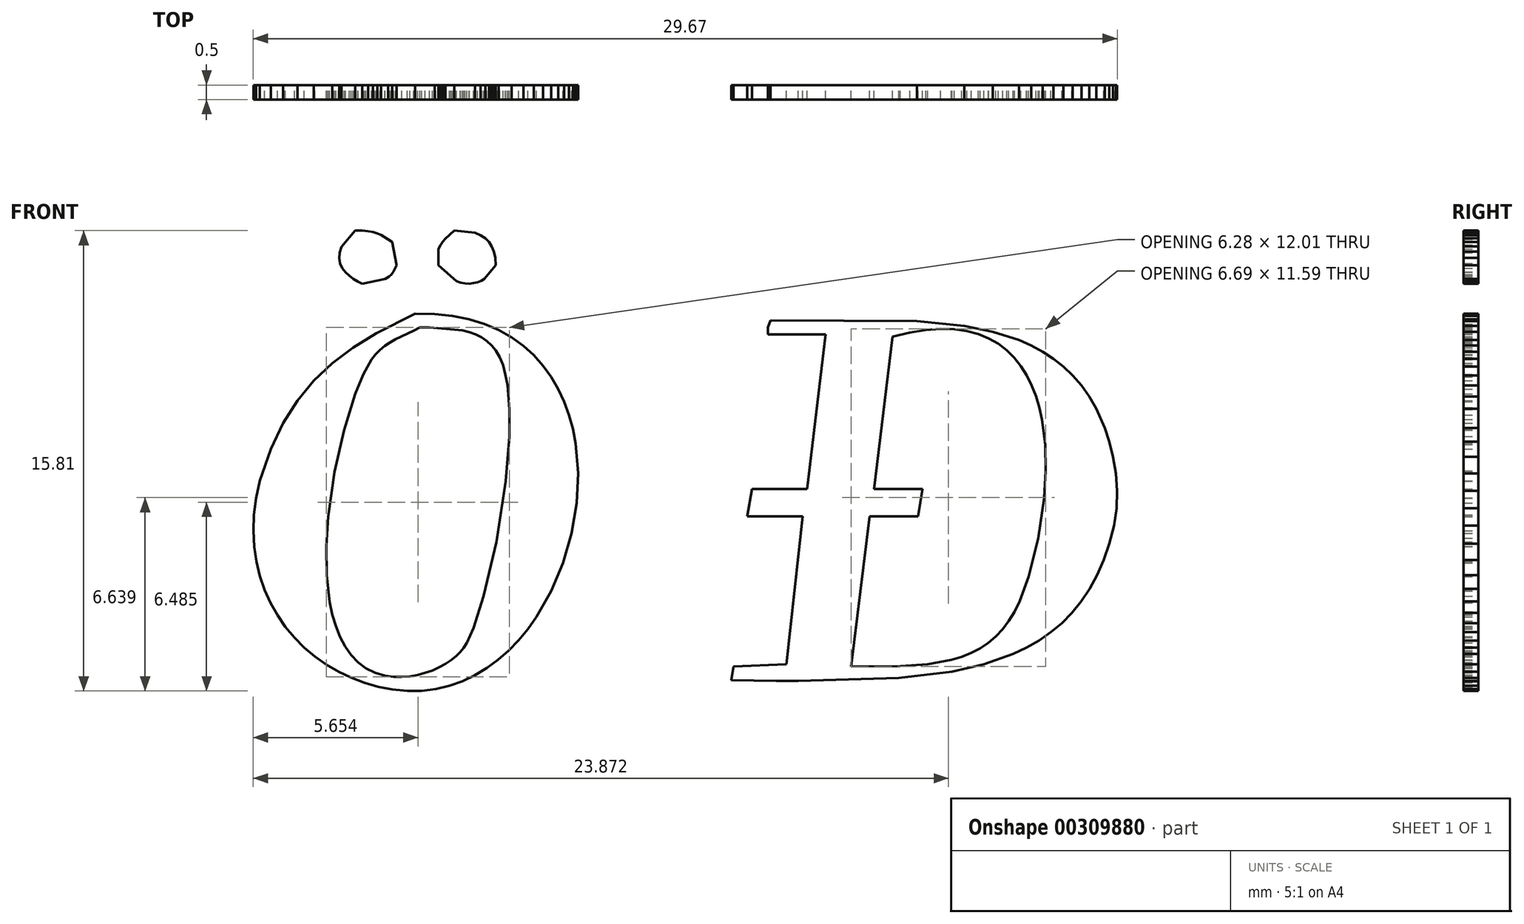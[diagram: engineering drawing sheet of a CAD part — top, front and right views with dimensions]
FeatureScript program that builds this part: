
annotation { "Feature Type Name" : "Feature", "Feature Type Description" : "" }
export const myFeature = defineFeature(function(context is Context, id is Id, definition is map)
    precondition{}
    {
        {
            var Q0;
            Q0=qCreatedBy(makeId("Front.planeOp"),FACE);
            var sketch = newSketch(context, id + "F0", { "sketchPlane" : qUnion([Q0])});
            skPoint(sketch, "E0.0", {"position": v(5.49, 5.53) * mm});
            skPoint(sketch, "E1.0", {"position": v(5.4, 5.3) * mm});
            skPoint(sketch, "E2.0", {"position": v(5.4, 5.06) * mm});
            skPoint(sketch, "E3.0", {"position": v(7.39, 5.06) * mm});
            skPoint(sketch, "E4.0", {"position": v(10.52, 5.52) * mm});
            skPoint(sketch, "E5.0", {"position": v(6.75, -0.25) * mm});
            skPoint(sketch, "E6.0", {"position": v(4.85, -0.25) * mm});
            skPoint(sketch, "E7.0", {"position": v(4.7, -1.2) * mm});
            skPoint(sketch, "E8.0", {"position": v(6.6, -1.2) * mm});
            skPoint(sketch, "E9.0", {"position": v(6.04, -6.27) * mm});
            skPoint(sketch, "E10.0", {"position": v(4.22, -6.35) * mm});
            skPoint(sketch, "E11.0", {"position": v(4.14, -6.82) * mm});
            skPoint(sketch, "E12.0", {"position": v(5.7, -6.84) * mm});
            skPoint(sketch, "E13.0", {"position": v(6.44, -6.84) * mm});
            skPoint(sketch, "E14.0", {"position": v(9.9, -6.75) * mm});
            skPoint(sketch, "E15.0", {"position": v(11.73, -6.52) * mm});
            skPoint(sketch, "E16.0", {"position": v(12.82, -6.27) * mm});
            skPoint(sketch, "E17.0", {"position": v(13.82, -5.92) * mm});
            skPoint(sketch, "E18.0", {"position": v(14.28, -5.7) * mm});
            skPoint(sketch, "E19.0", {"position": v(14.71, -5.46) * mm});
            skPoint(sketch, "E20.0", {"position": v(15.12, -5.17) * mm});
            skPoint(sketch, "E21.0", {"position": v(15.5, -4.86) * mm});
            skPoint(sketch, "E22.0", {"position": v(15.84, -4.5) * mm});
            skPoint(sketch, "E23.0", {"position": v(16.16, -4.12) * mm});
            skPoint(sketch, "E24.0", {"position": v(16.45, -3.69) * mm});
            skPoint(sketch, "E25.0", {"position": v(16.7, -3.21) * mm});
            skPoint(sketch, "E26.0", {"position": v(16.93, -2.7) * mm});
            skPoint(sketch, "E27.0", {"position": v(17.13, -2.13) * mm});
            skPoint(sketch, "E28.0", {"position": v(17.29, -1.52) * mm});
            skPoint(sketch, "E29.0", {"position": v(17.38, -0.92) * mm});
            skPoint(sketch, "E30.0", {"position": v(17.4, -0.31) * mm});
            skPoint(sketch, "E31.0", {"position": v(17.35, 0.28) * mm});
            skPoint(sketch, "E32.0", {"position": v(17.26, 0.85) * mm});
            skPoint(sketch, "E33.0", {"position": v(17.13, 1.37) * mm});
            skPoint(sketch, "E34.0", {"position": v(16.97, 1.84) * mm});
            skPoint(sketch, "E35.0", {"position": v(16.68, 2.5) * mm});
            skPoint(sketch, "E36.0", {"position": v(16.44, 2.92) * mm});
            skPoint(sketch, "E37.0", {"position": v(16.17, 3.3) * mm});
            skPoint(sketch, "E38.0", {"position": v(15.87, 3.64) * mm});
            skPoint(sketch, "E39.0", {"position": v(15.55, 3.95) * mm});
            skPoint(sketch, "E40.0", {"position": v(15.2, 4.22) * mm});
            skPoint(sketch, "E41.0", {"position": v(14.84, 4.46) * mm});
            skPoint(sketch, "E42.0", {"position": v(14.44, 4.67) * mm});
            skPoint(sketch, "E43.0", {"position": v(14.02, 4.86) * mm});
            skPoint(sketch, "E44.0", {"position": v(13.12, 5.15) * mm});
            skPoint(sketch, "E45.0", {"position": v(12.14, 5.35) * mm});
            skPoint(sketch, "E46.0", {"position": v(8.26, -6.35) * mm});
            skPoint(sketch, "E47.0", {"position": v(9.95, -6.34) * mm});
            skPoint(sketch, "E48.0", {"position": v(10.9, -6.27) * mm});
            skPoint(sketch, "E49.0", {"position": v(11.7, -6.12) * mm});
            skPoint(sketch, "E50.0", {"position": v(12.06, -6.01) * mm});
            skPoint(sketch, "E51.0", {"position": v(12.4, -5.88) * mm});
            skPoint(sketch, "E52.0", {"position": v(12.7, -5.73) * mm});
            skPoint(sketch, "E53.0", {"position": v(12.98, -5.54) * mm});
            skPoint(sketch, "E54.0", {"position": v(13.23, -5.32) * mm});
            skPoint(sketch, "E55.0", {"position": v(13.46, -5.07) * mm});
            skPoint(sketch, "E56.0", {"position": v(13.68, -4.79) * mm});
            skPoint(sketch, "E57.0", {"position": v(13.87, -4.47) * mm});
            skPoint(sketch, "E58.0", {"position": v(14.05, -4.1) * mm});
            skPoint(sketch, "E59.0", {"position": v(14.36, -3.26) * mm});
            skPoint(sketch, "E60.0", {"position": v(14.69, -1.94) * mm});
            skPoint(sketch, "E61.0", {"position": v(14.9, -0.56) * mm});
            skPoint(sketch, "E62.0", {"position": v(14.95, 0.36) * mm});
            skPoint(sketch, "E63.0", {"position": v(14.92, 1.27) * mm});
            skPoint(sketch, "E64.0", {"position": v(14.81, 2.13) * mm});
            skPoint(sketch, "E65.0", {"position": v(14.72, 2.54) * mm});
            skPoint(sketch, "E66.0", {"position": v(14.6, 2.93) * mm});
            skPoint(sketch, "E67.0", {"position": v(14.46, 3.3) * mm});
            skPoint(sketch, "E68.0", {"position": v(14.3, 3.64) * mm});
            skPoint(sketch, "E69.0", {"position": v(14.1, 3.96) * mm});
            skPoint(sketch, "E70.0", {"position": v(13.86, 4.25) * mm});
            skPoint(sketch, "E71.0", {"position": v(13.6, 4.5) * mm});
            skPoint(sketch, "E72.0", {"position": v(13.31, 4.73) * mm});
            skPoint(sketch, "E73.0", {"position": v(12.99, 4.92) * mm});
            skPoint(sketch, "E74.0", {"position": v(12.63, 5.07) * mm});
            skPoint(sketch, "E75.0", {"position": v(12.23, 5.17) * mm});
            skPoint(sketch, "E76.0", {"position": v(11.8, 5.23) * mm});
            skPoint(sketch, "E77.0", {"position": v(11.33, 5.25) * mm});
            skPoint(sketch, "E78.0", {"position": v(10.82, 5.2) * mm});
            skPoint(sketch, "E79.0", {"position": v(10.27, 5.12) * mm});
            skPoint(sketch, "E80.0", {"position": v(9.68, 4.98) * mm});
            skPoint(sketch, "E81.0", {"position": v(9.05, -0.25) * mm});
            skPoint(sketch, "E82.0", {"position": v(10.71, -0.25) * mm});
            skPoint(sketch, "E83.0", {"position": v(10.55, -1.2) * mm});
            skPoint(sketch, "E84.0", {"position": v(8.9, -1.2) * mm});
            skPoint(sketch, "E85.0", {"position": v(-5.36, 8.62) * mm});
            skPoint(sketch, "E86.0", {"position": v(-4.65, 8.54) * mm});
            skPoint(sketch, "E87.0", {"position": v(-4.46, 8.45) * mm});
            skPoint(sketch, "E88.0", {"position": v(-4.3, 8.35) * mm});
            skPoint(sketch, "E89.0", {"position": v(-4.18, 8.23) * mm});
            skPoint(sketch, "E90.0", {"position": v(-4.08, 8.08) * mm});
            skPoint(sketch, "E91.0", {"position": v(-4, 7.9) * mm});
            skPoint(sketch, "E92.0", {"position": v(-3.96, 7.69) * mm});
            skPoint(sketch, "E93.0", {"position": v(-3.94, 7.43) * mm});
            skPoint(sketch, "E94.0", {"position": v(-4.33, 6.96) * mm});
            skPoint(sketch, "E95.0", {"position": v(-4.44, 6.9) * mm});
            skPoint(sketch, "E96.0", {"position": v(-4.56, 6.85) * mm});
            skPoint(sketch, "E97.0", {"position": v(-4.7, 6.82) * mm});
            skPoint(sketch, "E98.0", {"position": v(-4.85, 6.8) * mm});
            skPoint(sketch, "E99.0", {"position": v(-5, 6.8) * mm});
            skPoint(sketch, "E100.0", {"position": v(-5.15, 6.83) * mm});
            skPoint(sketch, "E101.0", {"position": v(-5.28, 6.88) * mm});
            skPoint(sketch, "E102.0", {"position": v(-5.92, 7.43) * mm});
            skPoint(sketch, "E103.0", {"position": v(-5.92, 7.99) * mm});
            skPoint(sketch, "E104.0", {"position": v(-5.84, 8.13) * mm});
            skPoint(sketch, "E105.0", {"position": v(-5.76, 8.25) * mm});
            skPoint(sketch, "E106.0", {"position": v(-5.67, 8.34) * mm});
            skPoint(sketch, "E107.0", {"position": v(-7.5, 8.22) * mm});
            skPoint(sketch, "E108.0", {"position": v(-7.34, 7.43) * mm});
            skPoint(sketch, "E109.0", {"position": v(-7.47, 7.2) * mm});
            skPoint(sketch, "E110.0", {"position": v(-7.53, 7.11) * mm});
            skPoint(sketch, "E111.0", {"position": v(-7.62, 7.04) * mm});
            skPoint(sketch, "E112.0", {"position": v(-7.74, 6.96) * mm});
            skPoint(sketch, "E113.0", {"position": v(-8.53, 6.8) * mm});
            skPoint(sketch, "E114.0", {"position": v(-8.68, 6.87) * mm});
            skPoint(sketch, "E115.0", {"position": v(-8.83, 6.96) * mm});
            skPoint(sketch, "E116.0", {"position": v(-8.98, 7.07) * mm});
            skPoint(sketch, "E117.0", {"position": v(-9.1, 7.2) * mm});
            skPoint(sketch, "E118.0", {"position": v(-9.21, 7.33) * mm});
            skPoint(sketch, "E119.0", {"position": v(-9.29, 7.5) * mm});
            skPoint(sketch, "E120.0", {"position": v(-9.32, 7.67) * mm});
            skPoint(sketch, "E121.0", {"position": v(-9.3, 7.86) * mm});
            skPoint(sketch, "E122.0", {"position": v(-9.24, 8.07) * mm});
            skPoint(sketch, "E123.0", {"position": v(-8.77, 8.62) * mm});
            skPoint(sketch, "E124.0", {"position": v(-8.53, 8.62) * mm});
            skPoint(sketch, "E125.0", {"position": v(-8.33, 8.6) * mm});
            skPoint(sketch, "E126.0", {"position": v(-8.16, 8.57) * mm});
            skPoint(sketch, "E127.0", {"position": v(-8.01, 8.53) * mm});
            skPoint(sketch, "E128.0", {"position": v(-7.88, 8.47) * mm});
            skPoint(sketch, "E129.0", {"position": v(-7.64, 8.32) * mm});
            skPoint(sketch, "E130.0", {"position": v(-6.7, 5.77) * mm});
            skPoint(sketch, "E131.0", {"position": v(-6.04, 5.76) * mm});
            skPoint(sketch, "E132.0", {"position": v(-5.43, 5.7) * mm});
            skPoint(sketch, "E133.0", {"position": v(-4.85, 5.58) * mm});
            skPoint(sketch, "E134.0", {"position": v(-4.32, 5.41) * mm});
            skPoint(sketch, "E135.0", {"position": v(-3.84, 5.2) * mm});
            skPoint(sketch, "E136.0", {"position": v(-3.4, 4.95) * mm});
            skPoint(sketch, "E137.0", {"position": v(-3, 4.66) * mm});
            skPoint(sketch, "E138.0", {"position": v(-2.63, 4.34) * mm});
            skPoint(sketch, "E139.0", {"position": v(-2.31, 3.98) * mm});
            skPoint(sketch, "E140.0", {"position": v(-2.03, 3.6) * mm});
            skPoint(sketch, "E141.0", {"position": v(-1.8, 3.18) * mm});
            skPoint(sketch, "E142.0", {"position": v(-1.6, 2.74) * mm});
            skPoint(sketch, "E143.0", {"position": v(-1.42, 2.28) * mm});
            skPoint(sketch, "E144.0", {"position": v(-1.3, 1.8) * mm});
            skPoint(sketch, "E145.0", {"position": v(-1.2, 1.31) * mm});
            skPoint(sketch, "E146.0", {"position": v(-1.12, 0.3) * mm});
            skPoint(sketch, "E147.0", {"position": v(-1.16, -0.74) * mm});
            skPoint(sketch, "E148.0", {"position": v(-1.34, -1.78) * mm});
            skPoint(sketch, "E149.0", {"position": v(-1.63, -2.8) * mm});
            skPoint(sketch, "E150.0", {"position": v(-2.04, -3.76) * mm});
            skPoint(sketch, "E151.0", {"position": v(-2.55, -4.65) * mm});
            skPoint(sketch, "E152.0", {"position": v(-2.84, -5.06) * mm});
            skPoint(sketch, "E153.0", {"position": v(-3.16, -5.45) * mm});
            skPoint(sketch, "E154.0", {"position": v(-3.5, -5.8) * mm});
            skPoint(sketch, "E155.0", {"position": v(-3.87, -6.12) * mm});
            skPoint(sketch, "E156.0", {"position": v(-4.25, -6.4) * mm});
            skPoint(sketch, "E157.0", {"position": v(-4.66, -6.65) * mm});
            skPoint(sketch, "E158.0", {"position": v(-5.09, -6.86) * mm});
            skPoint(sketch, "E159.0", {"position": v(-5.54, -7.02) * mm});
            skPoint(sketch, "E160.0", {"position": v(-6, -7.13) * mm});
            skPoint(sketch, "E161.0", {"position": v(-6.49, -7.19) * mm});
            skPoint(sketch, "E162.0", {"position": v(-6.99, -7.2) * mm});
            skPoint(sketch, "E163.0", {"position": v(-7.5, -7.14) * mm});
            skPoint(sketch, "E164.0", {"position": v(-7.99, -7.04) * mm});
            skPoint(sketch, "E165.0", {"position": v(-8.46, -6.9) * mm});
            skPoint(sketch, "E166.0", {"position": v(-8.91, -6.74) * mm});
            skPoint(sketch, "E167.0", {"position": v(-9.35, -6.53) * mm});
            skPoint(sketch, "E168.0", {"position": v(-9.76, -6.28) * mm});
            skPoint(sketch, "E169.0", {"position": v(-10.15, -6) * mm});
            skPoint(sketch, "E170.0", {"position": v(-10.52, -5.7) * mm});
            skPoint(sketch, "E171.0", {"position": v(-10.86, -5.36) * mm});
            skPoint(sketch, "E172.0", {"position": v(-11.17, -4.99) * mm});
            skPoint(sketch, "E173.0", {"position": v(-11.44, -4.59) * mm});
            skPoint(sketch, "E174.0", {"position": v(-11.68, -4.17) * mm});
            skPoint(sketch, "E175.0", {"position": v(-11.88, -3.72) * mm});
            skPoint(sketch, "E176.0", {"position": v(-12.04, -3.24) * mm});
            skPoint(sketch, "E177.0", {"position": v(-12.16, -2.75) * mm});
            skPoint(sketch, "E178.0", {"position": v(-6.55, 5.3) * mm});
            skPoint(sketch, "E179.0", {"position": v(-6.22, 5.3) * mm});
            skPoint(sketch, "E180.0", {"position": v(-5.09, 5.2) * mm});
            skPoint(sketch, "E181.0", {"position": v(-4.85, 5.13) * mm});
            skPoint(sketch, "E182.0", {"position": v(-4.63, 5.05) * mm});
            skPoint(sketch, "E183.0", {"position": v(-4.43, 4.95) * mm});
            skPoint(sketch, "E184.0", {"position": v(-4.25, 4.83) * mm});
            skPoint(sketch, "E185.0", {"position": v(-4.08, 4.68) * mm});
            skPoint(sketch, "E186.0", {"position": v(-3.94, 4.5) * mm});
            skPoint(sketch, "E187.0", {"position": v(-3.8, 4.27) * mm});
            skPoint(sketch, "E188.0", {"position": v(-3.7, 4) * mm});
            skPoint(sketch, "E189.0", {"position": v(-3.6, 3.67) * mm});
            skPoint(sketch, "E190.0", {"position": v(-3.54, 3.31) * mm});
            skPoint(sketch, "E191.0", {"position": v(-3.48, 2.48) * mm});
            skPoint(sketch, "E192.0", {"position": v(-3.48, 1.55) * mm});
            skPoint(sketch, "E193.0", {"position": v(-3.6, 0.02) * mm});
            skPoint(sketch, "E194.0", {"position": v(-3.92, -2.06) * mm});
            skPoint(sketch, "E195.0", {"position": v(-4.36, -3.93) * mm});
            skPoint(sketch, "E196.0", {"position": v(-4.71, -5.02) * mm});
            skPoint(sketch, "E197.0", {"position": v(-4.94, -5.54) * mm});
            skPoint(sketch, "E198.0", {"position": v(-5.05, -5.71) * mm});
            skPoint(sketch, "E199.0", {"position": v(-5.16, -5.86) * mm});
            skPoint(sketch, "E200.0", {"position": v(-5.3, -6) * mm});
            skPoint(sketch, "E201.0", {"position": v(-5.48, -6.13) * mm});
            skPoint(sketch, "E202.0", {"position": v(-5.67, -6.26) * mm});
            skPoint(sketch, "E203.0", {"position": v(-5.89, -6.38) * mm});
            skPoint(sketch, "E204.0", {"position": v(-6.12, -6.48) * mm});
            skPoint(sketch, "E205.0", {"position": v(-6.37, -6.57) * mm});
            skPoint(sketch, "E206.0", {"position": v(-6.63, -6.64) * mm});
            skPoint(sketch, "E207.0", {"position": v(-6.9, -6.69) * mm});
            skPoint(sketch, "E208.0", {"position": v(-7.17, -6.7) * mm});
            skPoint(sketch, "E209.0", {"position": v(-7.46, -6.7) * mm});
            skPoint(sketch, "E210.0", {"position": v(-7.74, -6.66) * mm});
            skPoint(sketch, "E211.0", {"position": v(-8.09, -6.57) * mm});
            skPoint(sketch, "E212.0", {"position": v(-8.4, -6.41) * mm});
            skPoint(sketch, "E213.0", {"position": v(-8.67, -6.21) * mm});
            skPoint(sketch, "E214.0", {"position": v(-8.91, -5.96) * mm});
            skPoint(sketch, "E215.0", {"position": v(-9.12, -5.67) * mm});
            skPoint(sketch, "E216.0", {"position": v(-9.3, -5.33) * mm});
            skPoint(sketch, "E217.0", {"position": v(-9.44, -4.97) * mm});
            skPoint(sketch, "E218.0", {"position": v(-9.55, -4.57) * mm});
            skPoint(sketch, "E219.0", {"position": v(-9.64, -4.14) * mm});
            skPoint(sketch, "E220.0", {"position": v(-9.74, -3.22) * mm});
            skPoint(sketch, "E221.0", {"position": v(-9.76, -2.23) * mm});
            skPoint(sketch, "E222.0", {"position": v(-9.7, -1.2) * mm});
            skPoint(sketch, "E223.0", {"position": v(-9.48, 0.33) * mm});
            skPoint(sketch, "E224.0", {"position": v(-9.15, 1.77) * mm});
            skPoint(sketch, "E225.0", {"position": v(-8.76, 3.01) * mm});
            skPoint(sketch, "E226.0", {"position": v(-8.49, 3.68) * mm});
            skPoint(sketch, "E227.0", {"position": v(-8.21, 4.19) * mm});
            skPoint(sketch, "E228.0", {"position": v(-8.08, 4.37) * mm});
            skPoint(sketch, "E229.0", {"position": v(-7.92, 4.53) * mm});
            skPoint(sketch, "E230.0", {"position": v(-7.76, 4.66) * mm});
            skPoint(sketch, "E231.0", {"position": v(-7.58, 4.78) * mm});
            skPoint(sketch, "E232.0", {"position": v(-7.39, 4.89) * mm});
            skPoint(sketch, "E233.0", {"position": v(-6.77, 5.19) * mm});
            skPoint(sketch, "E234.0", {"position": v(-12.24, -2.23) * mm});
            skPoint(sketch, "E235.0", {"position": v(-12.27, -1.7) * mm});
            skPoint(sketch, "E236.0", {"position": v(-12.24, -1.14) * mm});
            skPoint(sketch, "E237.0", {"position": v(-12.17, -0.57) * mm});
            skPoint(sketch, "E238.0", {"position": v(-12.04, 0.02) * mm});
            skPoint(sketch, "E239.0", {"position": v(-11.67, 1.12) * mm});
            skPoint(sketch, "E240.0", {"position": v(-11.24, 2) * mm});
            skPoint(sketch, "E241.0", {"position": v(-10.75, 2.79) * mm});
            skPoint(sketch, "E242.0", {"position": v(-10.19, 3.47) * mm});
            skPoint(sketch, "E243.0", {"position": v(-9.55, 4.07) * mm});
            skPoint(sketch, "E244.0", {"position": v(-8.84, 4.6) * mm});
            skPoint(sketch, "E245.0", {"position": v(-8.05, 5.09) * mm});
            skLineSegment(sketch, "E246", {"start": v(13.12, 5.15) * mm, "end": v(14.02, 4.86) * mm});
            skLineSegment(sketch, "E247", {"start": v(14.02, 4.86) * mm, "end": v(14.44, 4.67) * mm});
            skLineSegment(sketch, "E248", {"start": v(14.44, 4.67) * mm, "end": v(14.84, 4.46) * mm});
            skLineSegment(sketch, "E249", {"start": v(14.84, 4.46) * mm, "end": v(15.2, 4.22) * mm});
            skLineSegment(sketch, "E250", {"start": v(15.2, 4.22) * mm, "end": v(15.55, 3.95) * mm});
            skLineSegment(sketch, "E251", {"start": v(15.55, 3.95) * mm, "end": v(15.87, 3.64) * mm});
            skLineSegment(sketch, "E252", {"start": v(15.87, 3.64) * mm, "end": v(16.17, 3.3) * mm});
            skLineSegment(sketch, "E253", {"start": v(16.17, 3.3) * mm, "end": v(16.44, 2.92) * mm});
            skLineSegment(sketch, "E254", {"start": v(16.44, 2.92) * mm, "end": v(16.68, 2.5) * mm});
            skLineSegment(sketch, "E255", {"start": v(16.68, 2.5) * mm, "end": v(16.97, 1.84) * mm});
            skLineSegment(sketch, "E256", {"start": v(16.97, 1.84) * mm, "end": v(17.13, 1.37) * mm});
            skLineSegment(sketch, "E257", {"start": v(17.13, 1.37) * mm, "end": v(17.26, 0.85) * mm});
            skLineSegment(sketch, "E258", {"start": v(17.26, 0.85) * mm, "end": v(17.35, 0.28) * mm});
            skLineSegment(sketch, "E259", {"start": v(17.35, 0.28) * mm, "end": v(17.4, -0.31) * mm});
            skLineSegment(sketch, "E260", {"start": v(17.4, -0.31) * mm, "end": v(17.38, -0.92) * mm});
            skLineSegment(sketch, "E261", {"start": v(17.38, -0.92) * mm, "end": v(17.29, -1.52) * mm});
            skLineSegment(sketch, "E262", {"start": v(17.29, -1.52) * mm, "end": v(17.13, -2.13) * mm});
            skLineSegment(sketch, "E263", {"start": v(17.13, -2.13) * mm, "end": v(16.93, -2.7) * mm});
            skLineSegment(sketch, "E264", {"start": v(16.93, -2.7) * mm, "end": v(16.7, -3.21) * mm});
            skLineSegment(sketch, "E265", {"start": v(16.7, -3.21) * mm, "end": v(16.45, -3.69) * mm});
            skLineSegment(sketch, "E266", {"start": v(16.45, -3.69) * mm, "end": v(16.16, -4.12) * mm});
            skLineSegment(sketch, "E267", {"start": v(16.16, -4.12) * mm, "end": v(15.84, -4.5) * mm});
            skLineSegment(sketch, "E268", {"start": v(15.84, -4.5) * mm, "end": v(15.5, -4.86) * mm});
            skLineSegment(sketch, "E269", {"start": v(15.5, -4.86) * mm, "end": v(15.12, -5.17) * mm});
            skLineSegment(sketch, "E270", {"start": v(15.12, -5.17) * mm, "end": v(14.71, -5.46) * mm});
            skLineSegment(sketch, "E271", {"start": v(14.71, -5.46) * mm, "end": v(14.28, -5.7) * mm});
            skLineSegment(sketch, "E272", {"start": v(14.28, -5.7) * mm, "end": v(13.82, -5.92) * mm});
            skLineSegment(sketch, "E273", {"start": v(13.82, -5.92) * mm, "end": v(12.82, -6.27) * mm});
            skLineSegment(sketch, "E274", {"start": v(12.82, -6.27) * mm, "end": v(11.73, -6.52) * mm});
            skLineSegment(sketch, "E275", {"start": v(11.73, -6.52) * mm, "end": v(9.9, -6.75) * mm});
            skLineSegment(sketch, "E276", {"start": v(9.9, -6.75) * mm, "end": v(6.44, -6.84) * mm});
            skLineSegment(sketch, "E277", {"start": v(6.44, -6.84) * mm, "end": v(5.7, -6.84) * mm});
            skLineSegment(sketch, "E278", {"start": v(5.7, -6.84) * mm, "end": v(4.14, -6.82) * mm});
            skLineSegment(sketch, "E279", {"start": v(4.14, -6.82) * mm, "end": v(4.22, -6.35) * mm});
            skLineSegment(sketch, "E280", {"start": v(4.22, -6.35) * mm, "end": v(6.04, -6.27) * mm});
            skLineSegment(sketch, "E281", {"start": v(6.04, -6.27) * mm, "end": v(6.6, -1.2) * mm});
            skLineSegment(sketch, "E282", {"start": v(6.6, -1.2) * mm, "end": v(4.7, -1.2) * mm});
            skLineSegment(sketch, "E283", {"start": v(4.7, -1.2) * mm, "end": v(4.85, -0.25) * mm});
            skLineSegment(sketch, "E284", {"start": v(4.85, -0.25) * mm, "end": v(6.75, -0.25) * mm});
            skLineSegment(sketch, "E285", {"start": v(6.75, -0.25) * mm, "end": v(7.39, 5.06) * mm});
            skLineSegment(sketch, "E286", {"start": v(7.39, 5.06) * mm, "end": v(5.4, 5.06) * mm});
            skLineSegment(sketch, "E287", {"start": v(5.4, 5.06) * mm, "end": v(5.4, 5.3) * mm});
            skLineSegment(sketch, "E288", {"start": v(5.4, 5.3) * mm, "end": v(5.49, 5.53) * mm});
            skLineSegment(sketch, "E289", {"start": v(5.49, 5.53) * mm, "end": v(10.52, 5.52) * mm});
            skLineSegment(sketch, "E290", {"start": v(10.52, 5.52) * mm, "end": v(12.14, 5.35) * mm});
            skLineSegment(sketch, "E291", {"start": v(12.14, 5.35) * mm, "end": v(13.12, 5.15) * mm});
            skLineSegment(sketch, "E292", {"start": v(9.05, -0.25) * mm, "end": v(9.68, 4.98) * mm});
            skLineSegment(sketch, "E293", {"start": v(9.68, 4.98) * mm, "end": v(10.27, 5.12) * mm});
            skLineSegment(sketch, "E294", {"start": v(10.27, 5.12) * mm, "end": v(10.82, 5.2) * mm});
            skLineSegment(sketch, "E295", {"start": v(10.82, 5.2) * mm, "end": v(11.33, 5.25) * mm});
            skLineSegment(sketch, "E296", {"start": v(11.33, 5.25) * mm, "end": v(11.8, 5.23) * mm});
            skLineSegment(sketch, "E297", {"start": v(11.8, 5.23) * mm, "end": v(12.23, 5.17) * mm});
            skLineSegment(sketch, "E298", {"start": v(12.23, 5.17) * mm, "end": v(12.63, 5.07) * mm});
            skLineSegment(sketch, "E299", {"start": v(12.63, 5.07) * mm, "end": v(12.99, 4.92) * mm});
            skLineSegment(sketch, "E300", {"start": v(12.99, 4.92) * mm, "end": v(13.31, 4.73) * mm});
            skLineSegment(sketch, "E301", {"start": v(13.31, 4.73) * mm, "end": v(13.6, 4.5) * mm});
            skLineSegment(sketch, "E302", {"start": v(13.6, 4.5) * mm, "end": v(13.86, 4.25) * mm});
            skLineSegment(sketch, "E303", {"start": v(13.86, 4.25) * mm, "end": v(14.1, 3.96) * mm});
            skLineSegment(sketch, "E304", {"start": v(14.1, 3.96) * mm, "end": v(14.3, 3.64) * mm});
            skLineSegment(sketch, "E305", {"start": v(14.3, 3.64) * mm, "end": v(14.46, 3.3) * mm});
            skLineSegment(sketch, "E306", {"start": v(14.46, 3.3) * mm, "end": v(14.6, 2.93) * mm});
            skLineSegment(sketch, "E307", {"start": v(14.6, 2.93) * mm, "end": v(14.72, 2.54) * mm});
            skLineSegment(sketch, "E308", {"start": v(14.72, 2.54) * mm, "end": v(14.81, 2.13) * mm});
            skLineSegment(sketch, "E309", {"start": v(14.81, 2.13) * mm, "end": v(14.92, 1.27) * mm});
            skLineSegment(sketch, "E310", {"start": v(14.92, 1.27) * mm, "end": v(14.95, 0.36) * mm});
            skLineSegment(sketch, "E311", {"start": v(14.95, 0.36) * mm, "end": v(14.9, -0.56) * mm});
            skLineSegment(sketch, "E312", {"start": v(14.9, -0.56) * mm, "end": v(14.69, -1.94) * mm});
            skLineSegment(sketch, "E313", {"start": v(14.69, -1.94) * mm, "end": v(14.36, -3.26) * mm});
            skLineSegment(sketch, "E314", {"start": v(14.36, -3.26) * mm, "end": v(14.05, -4.1) * mm});
            skLineSegment(sketch, "E315", {"start": v(14.05, -4.1) * mm, "end": v(13.87, -4.47) * mm});
            skLineSegment(sketch, "E316", {"start": v(13.87, -4.47) * mm, "end": v(13.68, -4.79) * mm});
            skLineSegment(sketch, "E317", {"start": v(13.68, -4.79) * mm, "end": v(13.46, -5.07) * mm});
            skLineSegment(sketch, "E318", {"start": v(13.46, -5.07) * mm, "end": v(13.23, -5.32) * mm});
            skLineSegment(sketch, "E319", {"start": v(13.23, -5.32) * mm, "end": v(12.98, -5.54) * mm});
            skLineSegment(sketch, "E320", {"start": v(12.98, -5.54) * mm, "end": v(12.7, -5.73) * mm});
            skLineSegment(sketch, "E321", {"start": v(12.7, -5.73) * mm, "end": v(12.4, -5.88) * mm});
            skLineSegment(sketch, "E322", {"start": v(12.4, -5.88) * mm, "end": v(12.06, -6.01) * mm});
            skLineSegment(sketch, "E323", {"start": v(12.06, -6.01) * mm, "end": v(11.7, -6.12) * mm});
            skLineSegment(sketch, "E324", {"start": v(11.7, -6.12) * mm, "end": v(10.9, -6.27) * mm});
            skLineSegment(sketch, "E325", {"start": v(10.9, -6.27) * mm, "end": v(9.95, -6.34) * mm});
            skLineSegment(sketch, "E326", {"start": v(9.95, -6.34) * mm, "end": v(8.26, -6.35) * mm});
            skLineSegment(sketch, "E327", {"start": v(8.26, -6.35) * mm, "end": v(8.9, -1.2) * mm});
            skLineSegment(sketch, "E328", {"start": v(8.9, -1.2) * mm, "end": v(10.55, -1.2) * mm});
            skLineSegment(sketch, "E329", {"start": v(10.55, -1.2) * mm, "end": v(10.71, -0.25) * mm});
            skLineSegment(sketch, "E330", {"start": v(10.71, -0.25) * mm, "end": v(9.05, -0.25) * mm});
            skLineSegment(sketch, "E331", {"start": v(-5.36, 8.62) * mm, "end": v(-4.65, 8.54) * mm});
            skLineSegment(sketch, "E332", {"start": v(-4.65, 8.54) * mm, "end": v(-4.46, 8.45) * mm});
            skLineSegment(sketch, "E333", {"start": v(-4.46, 8.45) * mm, "end": v(-4.3, 8.35) * mm});
            skLineSegment(sketch, "E334", {"start": v(-4.3, 8.35) * mm, "end": v(-4.18, 8.23) * mm});
            skLineSegment(sketch, "E335", {"start": v(-4.18, 8.23) * mm, "end": v(-4.08, 8.08) * mm});
            skLineSegment(sketch, "E336", {"start": v(-4.08, 8.08) * mm, "end": v(-4, 7.9) * mm});
            skLineSegment(sketch, "E337", {"start": v(-4, 7.9) * mm, "end": v(-3.96, 7.69) * mm});
            skLineSegment(sketch, "E338", {"start": v(-3.96, 7.69) * mm, "end": v(-3.94, 7.43) * mm});
            skLineSegment(sketch, "E339", {"start": v(-3.94, 7.43) * mm, "end": v(-4.33, 6.96) * mm});
            skLineSegment(sketch, "E340", {"start": v(-4.33, 6.96) * mm, "end": v(-4.44, 6.9) * mm});
            skLineSegment(sketch, "E341", {"start": v(-4.44, 6.9) * mm, "end": v(-4.56, 6.85) * mm});
            skLineSegment(sketch, "E342", {"start": v(-4.56, 6.85) * mm, "end": v(-4.7, 6.82) * mm});
            skLineSegment(sketch, "E343", {"start": v(-4.7, 6.82) * mm, "end": v(-4.85, 6.8) * mm});
            skLineSegment(sketch, "E344", {"start": v(-4.85, 6.8) * mm, "end": v(-5, 6.8) * mm});
            skLineSegment(sketch, "E345", {"start": v(-5, 6.8) * mm, "end": v(-5.15, 6.83) * mm});
            skLineSegment(sketch, "E346", {"start": v(-5.15, 6.83) * mm, "end": v(-5.28, 6.88) * mm});
            skLineSegment(sketch, "E347", {"start": v(-5.28, 6.88) * mm, "end": v(-5.92, 7.43) * mm});
            skLineSegment(sketch, "E348", {"start": v(-5.92, 7.43) * mm, "end": v(-5.92, 7.99) * mm});
            skLineSegment(sketch, "E349", {"start": v(-5.92, 7.99) * mm, "end": v(-5.84, 8.13) * mm});
            skLineSegment(sketch, "E350", {"start": v(-5.84, 8.13) * mm, "end": v(-5.76, 8.25) * mm});
            skLineSegment(sketch, "E351", {"start": v(-5.76, 8.25) * mm, "end": v(-5.67, 8.34) * mm});
            skLineSegment(sketch, "E352", {"start": v(-5.67, 8.34) * mm, "end": v(-5.36, 8.62) * mm});
            skLineSegment(sketch, "E353", {"start": v(-7.5, 8.22) * mm, "end": v(-7.34, 7.43) * mm});
            skLineSegment(sketch, "E354", {"start": v(-7.34, 7.43) * mm, "end": v(-7.47, 7.2) * mm});
            skLineSegment(sketch, "E355", {"start": v(-7.47, 7.2) * mm, "end": v(-7.53, 7.11) * mm});
            skLineSegment(sketch, "E356", {"start": v(-7.53, 7.11) * mm, "end": v(-7.62, 7.04) * mm});
            skLineSegment(sketch, "E357", {"start": v(-7.62, 7.04) * mm, "end": v(-7.74, 6.96) * mm});
            skLineSegment(sketch, "E358", {"start": v(-7.74, 6.96) * mm, "end": v(-8.53, 6.8) * mm});
            skLineSegment(sketch, "E359", {"start": v(-8.53, 6.8) * mm, "end": v(-8.68, 6.87) * mm});
            skLineSegment(sketch, "E360", {"start": v(-8.68, 6.87) * mm, "end": v(-8.83, 6.96) * mm});
            skLineSegment(sketch, "E361", {"start": v(-8.83, 6.96) * mm, "end": v(-8.98, 7.07) * mm});
            skLineSegment(sketch, "E362", {"start": v(-8.98, 7.07) * mm, "end": v(-9.1, 7.2) * mm});
            skLineSegment(sketch, "E363", {"start": v(-9.1, 7.2) * mm, "end": v(-9.21, 7.33) * mm});
            skLineSegment(sketch, "E364", {"start": v(-9.21, 7.33) * mm, "end": v(-9.29, 7.5) * mm});
            skLineSegment(sketch, "E365", {"start": v(-9.29, 7.5) * mm, "end": v(-9.32, 7.67) * mm});
            skLineSegment(sketch, "E366", {"start": v(-9.32, 7.67) * mm, "end": v(-9.3, 7.86) * mm});
            skLineSegment(sketch, "E367", {"start": v(-9.3, 7.86) * mm, "end": v(-9.24, 8.07) * mm});
            skLineSegment(sketch, "E368", {"start": v(-9.24, 8.07) * mm, "end": v(-8.77, 8.62) * mm});
            skLineSegment(sketch, "E369", {"start": v(-8.77, 8.62) * mm, "end": v(-8.53, 8.62) * mm});
            skLineSegment(sketch, "E370", {"start": v(-8.53, 8.62) * mm, "end": v(-8.33, 8.6) * mm});
            skLineSegment(sketch, "E371", {"start": v(-8.33, 8.6) * mm, "end": v(-8.16, 8.57) * mm});
            skLineSegment(sketch, "E372", {"start": v(-8.16, 8.57) * mm, "end": v(-8.01, 8.53) * mm});
            skLineSegment(sketch, "E373", {"start": v(-8.01, 8.53) * mm, "end": v(-7.88, 8.47) * mm});
            skLineSegment(sketch, "E374", {"start": v(-7.88, 8.47) * mm, "end": v(-7.64, 8.32) * mm});
            skLineSegment(sketch, "E375", {"start": v(-7.64, 8.32) * mm, "end": v(-7.5, 8.22) * mm});
            skLineSegment(sketch, "E376", {"start": v(-3.84, 5.2) * mm, "end": v(-3.4, 4.95) * mm});
            skLineSegment(sketch, "E377", {"start": v(-3.4, 4.95) * mm, "end": v(-3, 4.66) * mm});
            skLineSegment(sketch, "E378", {"start": v(-3, 4.66) * mm, "end": v(-2.63, 4.34) * mm});
            skLineSegment(sketch, "E379", {"start": v(-2.63, 4.34) * mm, "end": v(-2.31, 3.98) * mm});
            skLineSegment(sketch, "E380", {"start": v(-2.31, 3.98) * mm, "end": v(-2.03, 3.6) * mm});
            skLineSegment(sketch, "E381", {"start": v(-2.03, 3.6) * mm, "end": v(-1.8, 3.18) * mm});
            skLineSegment(sketch, "E382", {"start": v(-1.8, 3.18) * mm, "end": v(-1.6, 2.74) * mm});
            skLineSegment(sketch, "E383", {"start": v(-1.6, 2.74) * mm, "end": v(-1.42, 2.28) * mm});
            skLineSegment(sketch, "E384", {"start": v(-1.42, 2.28) * mm, "end": v(-1.3, 1.8) * mm});
            skLineSegment(sketch, "E385", {"start": v(-1.3, 1.8) * mm, "end": v(-1.2, 1.31) * mm});
            skLineSegment(sketch, "E386", {"start": v(-1.2, 1.31) * mm, "end": v(-1.12, 0.3) * mm});
            skLineSegment(sketch, "E387", {"start": v(-1.12, 0.3) * mm, "end": v(-1.16, -0.74) * mm});
            skLineSegment(sketch, "E388", {"start": v(-1.16, -0.74) * mm, "end": v(-1.34, -1.78) * mm});
            skLineSegment(sketch, "E389", {"start": v(-1.34, -1.78) * mm, "end": v(-1.63, -2.8) * mm});
            skLineSegment(sketch, "E390", {"start": v(-1.63, -2.8) * mm, "end": v(-2.04, -3.76) * mm});
            skLineSegment(sketch, "E391", {"start": v(-2.04, -3.76) * mm, "end": v(-2.55, -4.65) * mm});
            skLineSegment(sketch, "E392", {"start": v(-2.55, -4.65) * mm, "end": v(-2.84, -5.06) * mm});
            skLineSegment(sketch, "E393", {"start": v(-2.84, -5.06) * mm, "end": v(-3.16, -5.45) * mm});
            skLineSegment(sketch, "E394", {"start": v(-3.16, -5.45) * mm, "end": v(-3.5, -5.8) * mm});
            skLineSegment(sketch, "E395", {"start": v(-3.5, -5.8) * mm, "end": v(-3.87, -6.12) * mm});
            skLineSegment(sketch, "E396", {"start": v(-3.87, -6.12) * mm, "end": v(-4.25, -6.4) * mm});
            skLineSegment(sketch, "E397", {"start": v(-4.25, -6.4) * mm, "end": v(-4.66, -6.65) * mm});
            skLineSegment(sketch, "E398", {"start": v(-4.66, -6.65) * mm, "end": v(-5.09, -6.86) * mm});
            skLineSegment(sketch, "E399", {"start": v(-5.09, -6.86) * mm, "end": v(-5.54, -7.02) * mm});
            skLineSegment(sketch, "E400", {"start": v(-5.54, -7.02) * mm, "end": v(-6, -7.13) * mm});
            skLineSegment(sketch, "E401", {"start": v(-6, -7.13) * mm, "end": v(-6.49, -7.19) * mm});
            skLineSegment(sketch, "E402", {"start": v(-6.49, -7.19) * mm, "end": v(-6.99, -7.2) * mm});
            skLineSegment(sketch, "E403", {"start": v(-6.99, -7.2) * mm, "end": v(-7.5, -7.14) * mm});
            skLineSegment(sketch, "E404", {"start": v(-7.5, -7.14) * mm, "end": v(-7.99, -7.04) * mm});
            skLineSegment(sketch, "E405", {"start": v(-7.99, -7.04) * mm, "end": v(-8.46, -6.9) * mm});
            skLineSegment(sketch, "E406", {"start": v(-8.46, -6.9) * mm, "end": v(-8.91, -6.74) * mm});
            skLineSegment(sketch, "E407", {"start": v(-8.91, -6.74) * mm, "end": v(-9.35, -6.53) * mm});
            skLineSegment(sketch, "E408", {"start": v(-9.35, -6.53) * mm, "end": v(-9.76, -6.28) * mm});
            skLineSegment(sketch, "E409", {"start": v(-9.76, -6.28) * mm, "end": v(-10.15, -6) * mm});
            skLineSegment(sketch, "E410", {"start": v(-10.15, -6) * mm, "end": v(-10.52, -5.7) * mm});
            skLineSegment(sketch, "E411", {"start": v(-10.52, -5.7) * mm, "end": v(-10.86, -5.36) * mm});
            skLineSegment(sketch, "E412", {"start": v(-10.86, -5.36) * mm, "end": v(-11.17, -4.99) * mm});
            skLineSegment(sketch, "E413", {"start": v(-11.17, -4.99) * mm, "end": v(-11.44, -4.59) * mm});
            skLineSegment(sketch, "E414", {"start": v(-11.44, -4.59) * mm, "end": v(-11.68, -4.17) * mm});
            skLineSegment(sketch, "E415", {"start": v(-11.68, -4.17) * mm, "end": v(-11.88, -3.72) * mm});
            skLineSegment(sketch, "E416", {"start": v(-11.88, -3.72) * mm, "end": v(-12.04, -3.24) * mm});
            skLineSegment(sketch, "E417", {"start": v(-12.04, -3.24) * mm, "end": v(-12.16, -2.75) * mm});
            skLineSegment(sketch, "E418", {"start": v(-12.16, -2.75) * mm, "end": v(-12.24, -2.23) * mm});
            skLineSegment(sketch, "E419", {"start": v(-12.24, -2.23) * mm, "end": v(-12.27, -1.7) * mm});
            skLineSegment(sketch, "E420", {"start": v(-12.27, -1.7) * mm, "end": v(-12.24, -1.14) * mm});
            skLineSegment(sketch, "E421", {"start": v(-12.24, -1.14) * mm, "end": v(-12.17, -0.57) * mm});
            skLineSegment(sketch, "E422", {"start": v(-12.17, -0.57) * mm, "end": v(-12.04, 0.02) * mm});
            skLineSegment(sketch, "E423", {"start": v(-12.04, 0.02) * mm, "end": v(-11.67, 1.12) * mm});
            skLineSegment(sketch, "E424", {"start": v(-11.67, 1.12) * mm, "end": v(-11.24, 2) * mm});
            skLineSegment(sketch, "E425", {"start": v(-11.24, 2) * mm, "end": v(-10.75, 2.79) * mm});
            skLineSegment(sketch, "E426", {"start": v(-10.75, 2.79) * mm, "end": v(-10.19, 3.47) * mm});
            skLineSegment(sketch, "E427", {"start": v(-10.19, 3.47) * mm, "end": v(-9.55, 4.07) * mm});
            skLineSegment(sketch, "E428", {"start": v(-9.55, 4.07) * mm, "end": v(-8.84, 4.6) * mm});
            skLineSegment(sketch, "E429", {"start": v(-8.84, 4.6) * mm, "end": v(-8.05, 5.09) * mm});
            skLineSegment(sketch, "E430", {"start": v(-8.05, 5.09) * mm, "end": v(-6.7, 5.77) * mm});
            skLineSegment(sketch, "E431", {"start": v(-6.7, 5.77) * mm, "end": v(-6.04, 5.76) * mm});
            skLineSegment(sketch, "E432", {"start": v(-6.04, 5.76) * mm, "end": v(-5.43, 5.7) * mm});
            skLineSegment(sketch, "E433", {"start": v(-5.43, 5.7) * mm, "end": v(-4.85, 5.58) * mm});
            skLineSegment(sketch, "E434", {"start": v(-4.85, 5.58) * mm, "end": v(-4.32, 5.41) * mm});
            skLineSegment(sketch, "E435", {"start": v(-4.32, 5.41) * mm, "end": v(-3.84, 5.2) * mm});
            skLineSegment(sketch, "E436", {"start": v(-6.55, 5.3) * mm, "end": v(-6.22, 5.3) * mm});
            skLineSegment(sketch, "E437", {"start": v(-6.22, 5.3) * mm, "end": v(-5.09, 5.2) * mm});
            skLineSegment(sketch, "E438", {"start": v(-5.09, 5.2) * mm, "end": v(-4.85, 5.13) * mm});
            skLineSegment(sketch, "E439", {"start": v(-4.85, 5.13) * mm, "end": v(-4.63, 5.05) * mm});
            skLineSegment(sketch, "E440", {"start": v(-4.63, 5.05) * mm, "end": v(-4.43, 4.95) * mm});
            skLineSegment(sketch, "E441", {"start": v(-4.43, 4.95) * mm, "end": v(-4.25, 4.83) * mm});
            skLineSegment(sketch, "E442", {"start": v(-4.25, 4.83) * mm, "end": v(-4.08, 4.68) * mm});
            skLineSegment(sketch, "E443", {"start": v(-4.08, 4.68) * mm, "end": v(-3.94, 4.5) * mm});
            skLineSegment(sketch, "E444", {"start": v(-3.94, 4.5) * mm, "end": v(-3.8, 4.27) * mm});
            skLineSegment(sketch, "E445", {"start": v(-3.8, 4.27) * mm, "end": v(-3.7, 4) * mm});
            skLineSegment(sketch, "E446", {"start": v(-3.7, 4) * mm, "end": v(-3.6, 3.67) * mm});
            skLineSegment(sketch, "E447", {"start": v(-3.6, 3.67) * mm, "end": v(-3.54, 3.31) * mm});
            skLineSegment(sketch, "E448", {"start": v(-3.54, 3.31) * mm, "end": v(-3.48, 2.48) * mm});
            skLineSegment(sketch, "E449", {"start": v(-3.48, 2.48) * mm, "end": v(-3.48, 1.55) * mm});
            skLineSegment(sketch, "E450", {"start": v(-3.48, 1.55) * mm, "end": v(-3.6, 0.02) * mm});
            skLineSegment(sketch, "E451", {"start": v(-3.6, 0.02) * mm, "end": v(-3.92, -2.06) * mm});
            skLineSegment(sketch, "E452", {"start": v(-3.92, -2.06) * mm, "end": v(-4.36, -3.93) * mm});
            skLineSegment(sketch, "E453", {"start": v(-4.36, -3.93) * mm, "end": v(-4.71, -5.02) * mm});
            skLineSegment(sketch, "E454", {"start": v(-4.71, -5.02) * mm, "end": v(-4.94, -5.54) * mm});
            skLineSegment(sketch, "E455", {"start": v(-4.94, -5.54) * mm, "end": v(-5.05, -5.71) * mm});
            skLineSegment(sketch, "E456", {"start": v(-5.05, -5.71) * mm, "end": v(-5.16, -5.86) * mm});
            skLineSegment(sketch, "E457", {"start": v(-5.16, -5.86) * mm, "end": v(-5.3, -6) * mm});
            skLineSegment(sketch, "E458", {"start": v(-5.3, -6) * mm, "end": v(-5.48, -6.13) * mm});
            skLineSegment(sketch, "E459", {"start": v(-5.48, -6.13) * mm, "end": v(-5.67, -6.26) * mm});
            skLineSegment(sketch, "E460", {"start": v(-5.67, -6.26) * mm, "end": v(-5.89, -6.38) * mm});
            skLineSegment(sketch, "E461", {"start": v(-5.89, -6.38) * mm, "end": v(-6.12, -6.48) * mm});
            skLineSegment(sketch, "E462", {"start": v(-6.12, -6.48) * mm, "end": v(-6.37, -6.57) * mm});
            skLineSegment(sketch, "E463", {"start": v(-6.37, -6.57) * mm, "end": v(-6.63, -6.64) * mm});
            skLineSegment(sketch, "E464", {"start": v(-6.63, -6.64) * mm, "end": v(-6.9, -6.69) * mm});
            skLineSegment(sketch, "E465", {"start": v(-6.9, -6.69) * mm, "end": v(-7.17, -6.7) * mm});
            skLineSegment(sketch, "E466", {"start": v(-7.74, -6.66) * mm, "end": v(-7.46, -6.7) * mm});
            skLineSegment(sketch, "E467", {"start": v(-7.46, -6.7) * mm, "end": v(-7.17, -6.7) * mm});
            skLineSegment(sketch, "E468", {"start": v(-7.74, -6.66) * mm, "end": v(-8.09, -6.57) * mm});
            skLineSegment(sketch, "E469", {"start": v(-8.09, -6.57) * mm, "end": v(-8.4, -6.41) * mm});
            skLineSegment(sketch, "E470", {"start": v(-8.4, -6.41) * mm, "end": v(-8.67, -6.21) * mm});
            skLineSegment(sketch, "E471", {"start": v(-9.44, -4.97) * mm, "end": v(-9.3, -5.33) * mm});
            skLineSegment(sketch, "E472", {"start": v(-9.3, -5.33) * mm, "end": v(-9.12, -5.67) * mm});
            skLineSegment(sketch, "E473", {"start": v(-9.12, -5.67) * mm, "end": v(-8.91, -5.96) * mm});
            skLineSegment(sketch, "E474", {"start": v(-8.91, -5.96) * mm, "end": v(-8.67, -6.21) * mm});
            skLineSegment(sketch, "E475", {"start": v(-9.44, -4.97) * mm, "end": v(-9.55, -4.57) * mm});
            skLineSegment(sketch, "E476", {"start": v(-9.55, -4.57) * mm, "end": v(-9.64, -4.14) * mm});
            skLineSegment(sketch, "E477", {"start": v(-9.74, -3.22) * mm, "end": v(-9.64, -4.14) * mm});
            skLineSegment(sketch, "E478", {"start": v(-9.76, -2.23) * mm, "end": v(-9.74, -3.22) * mm});
            skLineSegment(sketch, "E479", {"start": v(-9.7, -1.2) * mm, "end": v(-9.76, -2.23) * mm});
            skLineSegment(sketch, "E480", {"start": v(-9.48, 0.33) * mm, "end": v(-9.7, -1.2) * mm});
            skLineSegment(sketch, "E481", {"start": v(-9.15, 1.77) * mm, "end": v(-9.48, 0.33) * mm});
            skLineSegment(sketch, "E482", {"start": v(-8.76, 3.01) * mm, "end": v(-9.15, 1.77) * mm});
            skLineSegment(sketch, "E483", {"start": v(-6.55, 5.3) * mm, "end": v(-6.77, 5.19) * mm});
            skLineSegment(sketch, "E484", {"start": v(-6.77, 5.19) * mm, "end": v(-7.39, 4.89) * mm});
            skLineSegment(sketch, "E485", {"start": v(-7.39, 4.89) * mm, "end": v(-7.58, 4.78) * mm});
            skLineSegment(sketch, "E486", {"start": v(-7.58, 4.78) * mm, "end": v(-7.76, 4.66) * mm});
            skLineSegment(sketch, "E487", {"start": v(-7.76, 4.66) * mm, "end": v(-7.92, 4.53) * mm});
            skLineSegment(sketch, "E488", {"start": v(-7.92, 4.53) * mm, "end": v(-8.08, 4.37) * mm});
            skLineSegment(sketch, "E489", {"start": v(-8.08, 4.37) * mm, "end": v(-8.21, 4.19) * mm});
            skLineSegment(sketch, "E490", {"start": v(-8.21, 4.19) * mm, "end": v(-8.49, 3.68) * mm});
            skLineSegment(sketch, "E491", {"start": v(-8.49, 3.68) * mm, "end": v(-8.76, 3.01) * mm});
            skSolve(sketch);
        }
        {
            var Q0;
            Q0=makeQuery(id+"F0.imprint","IMPRINT",FACE,{"disambiguationData":[TD([[makeQuery(id+"F0.imprint","IMPRINT",EDGE,{"derivedFrom":sQuery(id+"F0.wireOp",EDGE,"E376")}),-1.0]])]});
            var Q1;
            Q1=makeQuery(id+"F0.imprint","IMPRINT",FACE,{"disambiguationData":[TD([[makeQuery(id+"F0.imprint","IMPRINT",EDGE,{"derivedFrom":sQuery(id+"F0.wireOp",EDGE,"E331")}),-1.0]])]});
            var Q2;
            Q2=makeQuery(id+"F0.imprint","IMPRINT",FACE,{"disambiguationData":[TD([[makeQuery(id+"F0.imprint","IMPRINT",EDGE,{"derivedFrom":sQuery(id+"F0.wireOp",EDGE,"E353")}),-1.0]])]});
            var Q3;
            Q3=makeQuery(id+"F0.imprint","IMPRINT",FACE,{"disambiguationData":[TD([[makeQuery(id+"F0.imprint","IMPRINT",EDGE,{"derivedFrom":sQuery(id+"F0.wireOp",EDGE,"E246")}),-1.0]])]});
            extrude(context, id + "F1", {"entities" : qUnion([Q0, Q1, Q2, Q3]), "depth" : 0.5 * mm});
        }
    });
